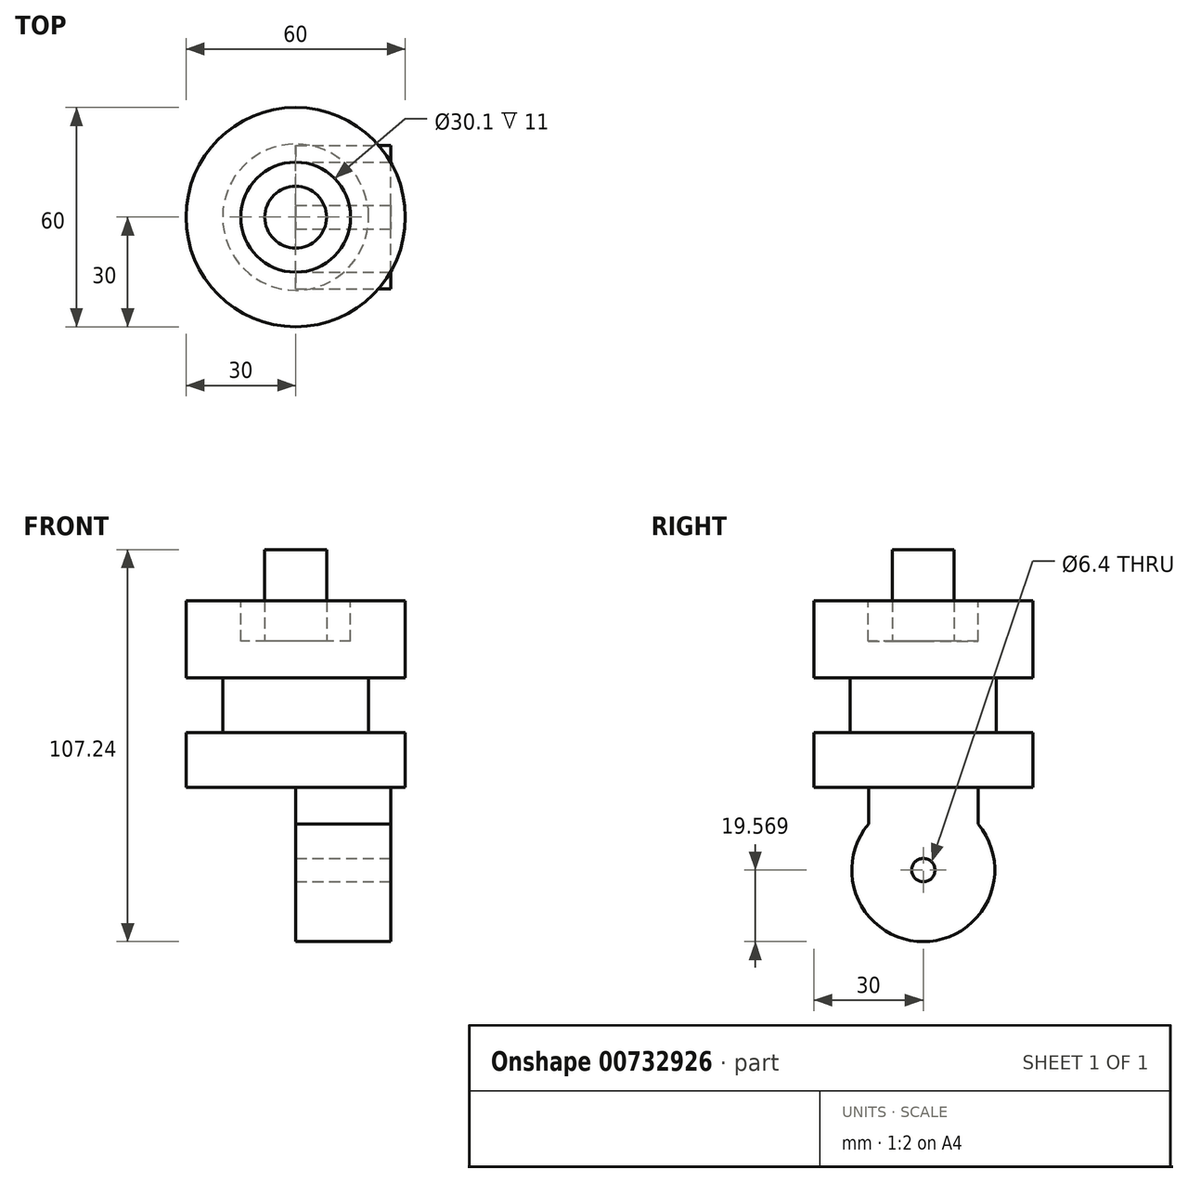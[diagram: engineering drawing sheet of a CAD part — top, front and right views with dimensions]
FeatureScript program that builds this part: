
annotation { "Feature Type Name" : "Feature", "Feature Type Description" : "" }
export const myFeature = defineFeature(function(context is Context, id is Id, definition is map)
    precondition{}
    {
        {
            var Q0;
            Q0=qCreatedBy(makeId("Top.planeOp"),FACE);
            var sketch = newSketch(context, id + "F0", { "sketchPlane" : qUnion([Q0])});
            skCircle(sketch, "E0", {"center": v(0, 0) * mm, "radius": 30 * mm});
            skSolve(sketch);
        }
        {
            var Q0;
            Q0=qSketchRegion(id+"F0",true);
            extrude(context, id + "F1", {"entities" : qUnion([Q0]), "depth" : 15 * mm, "offsetDistance" : 25 * mm});
        }
        {
            var Q0;
            Q0=makeQuery(id+"F1.opExtrude","CAP_FACE",FACE,{"disambiguationData":[OSD([sQuery(id+"F0.wireOp",EDGE,"E0")])],"isStart":false});
            var sketch = newSketch(context, id + "F2", { "sketchPlane" : qUnion([Q0])});
            skCircle(sketch, "E1", {"center": v(0, 0) * mm, "radius": 15.05 * mm});
            skSolve(sketch);
        }
        {
            var Q0;
            Q0=qSketchRegion(id+"F2",true);
            extrude(context, id + "F3", {"entities" : qUnion([Q0]), "operationType" : NewBodyOperationType.REMOVE, "oppositeDirection" : true, "depth" : 5 * mm, "offsetDistance" : 25 * mm});
        }
        {
            var Q0;
            Q0=makeQuery(id+"F1.opExtrude","CAP_FACE",FACE,{"disambiguationData":[OSD([sQuery(id+"F0.wireOp",EDGE,"E0")])],"isStart":false});
            extrude(context, id + "F4", {"entities" : qUnion([Q0]), "operationType" : NewBodyOperationType.ADD, "depth" : 6 * mm, "offsetDistance" : 25 * mm});
        }
        {
            var Q0;
            Q0=makeQuery(id+"F1.opExtrude","CAP_FACE",FACE,{"disambiguationData":[OSD([sQuery(id+"F0.wireOp",EDGE,"E0")])],"isStart":true});
            var sketch = newSketch(context, id + "F5", { "sketchPlane" : qUnion([Q0])});
            skCircle(sketch, "E2", {"center": v(0, 0) * mm, "radius": 20 * mm});
            skSolve(sketch);
        }
        {
            var Q0;
            Q0 = qSketchRegion(id + "F5", true);
            extrude(context, id + "F6", {"entities" : qUnion([Q0]), "operationType" : NewBodyOperationType.ADD, "depth" : 15 * mm, "offsetDistance" : 25 * mm});
        }
        {
            var Q0;
            Q0=makeQuery(id+"F6.opExtrude","CAP_FACE",FACE,{"disambiguationData":[OSD([sQuery(id+"F5.wireOp",EDGE,"E2")])],"isStart":false});
            var sketch = newSketch(context, id + "F7", { "sketchPlane" : qUnion([Q0])});
            skCircle(sketch, "E3", {"center": v(0, 0) * mm, "radius": 30 * mm});
            skSolve(sketch);
        }
        {
            var Q0;
            Q0=makeQuery(id+"F7.imprint","IMPRINT",FACE,{"disambiguationData":[TD([[makeQuery(id+"F7.imprint","IMPRINT",EDGE,{"derivedFrom":sQuery(id+"F7.wireOp",EDGE,"E3")}),1.0]])]});
            var Q1;
            Q1=makeQuery(id+"F7.imprint","IMPRINT",FACE,{"disambiguationData":[TD([[makeQuery(id+"F7.imprint","IMPRINT",EDGE,{"derivedFrom":makeQuery(id+"F6.opExtrude","CAP_EDGE",EDGE,{"disambiguationData":[OSD([sQuery(id+"F5.wireOp",EDGE,"E2")])],"isStart":false})}),1.0]])]});
            extrude(context, id + "F8", {"entities" : qUnion([Q0, Q1]), "operationType" : NewBodyOperationType.ADD, "depth" : 15 * mm, "offsetDistance" : 25 * mm});
        }
        {
            var Q0;
            Q0=makeQuery(id+"F8.opExtrude","CAP_FACE",FACE,{"disambiguationData":[OSD([sQuery(id+"F7.wireOp",EDGE,"E3")])],"isStart":false});
            var sketch = newSketch(context, id + "F9", { "sketchPlane" : qUnion([Q0])});
            skLineSegment(sketch, "E4.bottom", {"start": v(-25.98, 15) * mm, "end": v(0, 15) * mm});
            skLineSegment(sketch, "E4.top", {"start": v(-25.98, -15) * mm, "end": v(0, -15) * mm});
            skLineSegment(sketch, "E4.left", {"start": v(-25.98, 15) * mm, "end": v(-25.98, -15) * mm});
            skLineSegment(sketch, "E4.right", {"start": v(25.98, 15) * mm, "end": v(25.98, -15) * mm});
            skPoint(sketch, "E4.middle", {"position": v(0, 0) * mm});
            skLineSegment(sketch, "E5", {"start": v(0, 15) * mm, "end": v(0, -15) * mm});
            skLineSegment(sketch, "E6", {"start": v(0, 15) * mm, "end": v(13, 15) * mm});
            skLineSegment(sketch, "E7", {"start": v(0, -15) * mm, "end": v(25.98, -15) * mm});
            skLineSegment(sketch, "E8", {"start": v(-13, 15) * mm, "end": v(-13, -15) * mm});
            skLineSegment(sketch, "E9", {"start": v(13, 15) * mm, "end": v(13, -15) * mm});
            skLineSegment(sketch, "E10", {"start": v(13, 15) * mm, "end": v(25.98, 15) * mm});
            skSolve(sketch);
        }
        {
            var Q0;
            {var subQ0=sQuery(id+"F9.wireOp",EDGE,"E5");Q0=makeQuery(id+"F9.imprint","IMPRINT",FACE,{"disambiguationData":[TD([[makeQuery(id+"F9.imprint","IMPRINT",EDGE,{"derivedFrom":subQ0}),1.0]])]});}
            var Q1;
            {var subQ0=sQuery(id+"F9.wireOp",EDGE,"E4.right");Q1=makeQuery(id+"F9.imprint","IMPRINT",FACE,{"disambiguationData":[TD([[makeQuery(id+"F9.imprint","IMPRINT",EDGE,{"derivedFrom":subQ0}),-1.0]])]});}
            extrude(context, id + "F10", {"entities" : qUnion([Q0, Q1]), "operationType" : NewBodyOperationType.ADD, "depth" : 10.1 * mm, "offsetDistance" : 25 * mm});
        }
        {
            var Q0;
            Q0=makeQuery(id+"F10.opExtrude","SWEPT_FACE",FACE,{"disambiguationData":[OSD([sQuery(id+"F9.wireOp",EDGE,"E4.right")])]});
            var sketch = newSketch(context, id + "F11", { "sketchPlane" : qUnion([Q0])});
            skLineSegment(sketch, "E11", {"start": v(0, -40.1) * mm, "end": v(0, -33.1) * mm});
            skCircle(sketch, "E12", {"center": v(0, -52.67) * mm, "radius": 19.57 * mm});
            skPoint(sketch, "E12.first.point", {"position": v(-15, -40.1) * mm});
            skPoint(sketch, "E12.third.point", {"position": v(-15, -40.1) * mm});
            skCircle(sketch, "E13", {"center": v(0, -52.67) * mm, "radius": 3.2 * mm});
            skSolve(sketch);
        }
        {
            var Q0;
            Q0=makeQuery(id+"F11.imprint","IMPRINT",FACE,{"disambiguationData":[TD([[makeQuery(id+"F11.imprint","IMPRINT",EDGE,{"derivedFrom":sQuery(id+"F11.wireOp",EDGE,"E13")}),-1.0]])]});
            extrude(context, id + "F12", {"entities" : qUnion([Q0]), "operationType" : NewBodyOperationType.ADD, "oppositeDirection" : true, "depth" : 25.98 * mm, "offsetDistance" : 25 * mm});
        }
        {
            var Q0;
            Q0=makeQuery(id+"F3.boolean.opBoolean","COPY",FACE,{"derivedFrom":makeQuery(id+"F3.opExtrude","CAP_FACE",FACE,{"disambiguationData":[OSD([sQuery(id+"F2.wireOp",EDGE,"E1")])],"isStart":false})});
            var sketch = newSketch(context, id + "F13", { "sketchPlane" : qUnion([Q0])});
            skCircle(sketch, "E14", {"center": v(0, 0) * mm, "radius": 8.45 * mm});
            skSolve(sketch);
        }
        {
            var Q0;
            Q0 = qSketchRegion(id + "F13", true);
            extrude(context, id + "F14", {"entities" : qUnion([Q0]), "operationType" : NewBodyOperationType.ADD, "depth" : 25 * mm, "offsetDistance" : 25 * mm});
        }
    });
